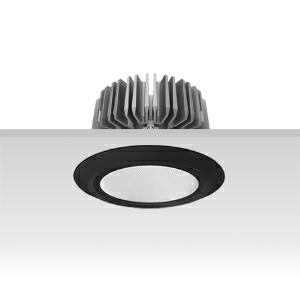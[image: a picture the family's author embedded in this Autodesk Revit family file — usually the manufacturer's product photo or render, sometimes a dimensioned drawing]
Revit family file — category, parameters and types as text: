
# Revit family: 3f_filippi_-_3f_reno_bianco_ampio_3f_filippi_-_30362_a01047_-_3f_reno_150_wh_2000-930_ep_wide___smp_bk_7f42
name_source: partatom
category: Lighting Fixtures
units: mm (PartAtom-declared; Revit-internal decimal feet)

## family parameters
Cut with Voids When Loaded = No
Host = Face
Light Source = No
Part Type = Normal
Room Calculation Point = No
Round Connector Dimension = Use Diameter
Shared = No

## types (1)
- 3F Filippi - 3F Reno Bianco Ampio (1 x LED, 1652 lm, 25 W, 3000 K)
    Apparent Load = 25 VA
    Approval mark = ENEC
    CIE Flux Codes = 73 92 98 100 100
    Color Rendering = 90
    Color Temperature = 3000 K
    Control Gear = Electronic ballast
    Default Elevation = 1800 mm
    Description = ILLUMINOTECHNICAL
Luminous efficiency 100% (DLOR 100%, ULOR 0%).
Initial luminous flux of the luminaire 1652 lm.
Emergency luminaire luminous flux BLF 16.7%.
Direct symmetric wide distribution.
Installation Interdistance Transv.D = 1.01 x hu - Long.D = 1.00 x hu.
Tabular UGR (CIE 117 - 4H-8H; S=0.25H; 70/50/20): RUG 23.3 - 23.3.
Beam angle: 70° - 70°.
Luminous efficacy 66 lm/W.
Lifetime (L90/B10): 30000 h. (tq+25°C)
Lifetime (L85/B10): 50000 h. (tq+25°C)
Lifetime (L70/B10): 80000 h. (tq+25°C)
Sudden decreased luminous flux after 50000 hours: 0% (C0).
Photobiological safety in compliance with IEC/TR 62778: RG0 risk exempt, (IEC 62471).
In compliance with IEC/EN 62722-2-1 - IEC/EN 62717 standards.

SOURCE
Compact LED module 2000/930.
Energy efficiency class (UE 2019/2020 - UE 2019/2015): E.
CIE 13.3 Colour rendering index: CRI >90 (R9 >50%).
IES TM-30 Fidelity Index: Rf = 92 Rg = 101.
CCT nominal colour temperature 3000 K.
Colour initial tolerance (MacAdam): SDCM 3.
Zhaga Book 3 compliant.

MECHANICAL
Passive heat dissipator in die-casting aluminium, oversized, for optimum thermal management of the LED module.
Parabolic element with graduated/concentric rings in white polycarbonate.
Transparent external lens with glossy and satin differentiated surfaces, with a cooling and anti-insect system in methacrylate (PMMA).
Fastening spring clips in stainless steel.
Dimensions: diameter 176 mm, height 111 mm. Weight 1.29 kg.
IP44 protection degree for exposed part, IP20 for recessed part.
Mechanical strength to impacts IK05 (0.7 joule).
Glow-wire test resistance 650°C.

ELECTRICAL
Wiring on a separate unit.
Halogen Free electronic wiring 230V-50/60Hz, power factor 0.90, THD <25%, constant output current, SELV, class II, 1 driver.
Power of the luminaire 25 W.
CE - IEC 60598-1 - EN 60598-1.
EP maintained emergency wiring on board, 1h duration, 24h recharge; compliant with EN 60598-2-22, excluding high risk areas.
SAFE FLICKER: PstLM=<1 and SVM=<0.4 (IEC TR 61547-1 and IEC TR 63158), to ensure a more comfortable and safe light.
Ambient temperature from +5°C to +25°C.
Temperature class T6 max 85°C.
Relative humidity UR: <85%.

INSTALLATION
Pull-up recessed fitting.
False ceiling carving: 150 mm.
All accessories dedicated to this product are available on the Catalog and on our website www.3F-Filippi.com.

ACCESSORIES
A01047 - Anti-glare microprismatic SMP diffuser in methacrylate (PMMA), locked and in line with the trim, in black polycarbonate.

APPLICATIONS
Suitable product for food production plants (HACCP), IFS (Food Version 6), BRC (GSFS Food Version 7).
Environments: architectural, commercial, exhibition areas, transit areas, corridors, shops, display windows, service areas.
In false ceilings with narrow voids.

WARNING
Luminaire designed for disposal/recycling at end-of-life.
Replaceable (LED only) light source by a professional. Replaceable control gear by a professional.
    Height = 0 mm  [stored 0 ft]
    Lamp = 1 x LED
    Lamp Light Flux = 1652 lm
    Lamp Power = 25 W
    Lamp count = 1
    Length = 176 mm
    Lifetime = 50000 h
    Luminous efficacy = 66 lm/W
    Manufacturer = 3F Filippi
    ModVariant = No
    Model = 3F Filippi - 30362+A01047 - 3F Reno 150 WH 2000-930 EP WIDE + SMP BK
    Mounting Place = Ceiling
    Mounting Type = Recessed
    Number of Poles = 1
    OnlyDefault = Yes
    Power Factor = 1
    Product Name = 3F Filippi - 3F Reno Bianco Ampio
    Product group = recessed luminaire
    ProductGroupID = 4
    Protection Class = Protection class II
    Protection Degree = IP 20
    RLX_Detail_Level = 1
    RLX_Emergency_Light_Flux = 0 lm
    RLX_Emergency_Type = 0
    RLX_Emergency_Type_DB = No
    RlxData = <blob elided: 85757 chars, md5=a3560fd2>
    Socket = socket
    Standby Power = 0 W
    System Light Flux = 1652 lm
    System Power = 25 W
    Type Comments = Product without accessories
    Type Image = 3ffilippi_3f_reno_150_bk_vs_smp.jpg
    URL = http://relux.com
    VarID = ---
    Voltage = 0 V
    Weight = 0.00 kg
    Width = 0 mm  [stored 0 ft]

note: [stored X ft] marks values corroborated as IEEE doubles in the binary element streams (Revit-internal decimal feet)

## geometry (parser evidence)
native form markers: Blend x4, Sweep x11
no freeform markers — native parametric forms only
